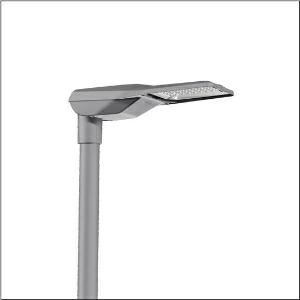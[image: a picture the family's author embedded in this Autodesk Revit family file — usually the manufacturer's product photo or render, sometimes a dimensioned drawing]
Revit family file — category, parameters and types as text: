
# Revit family: streetlight_sl_21_mini___st0_8a_5xe6c43a08gb_7bc1
name_source: partatom
category: Lighting Fixtures
units: mm (PartAtom-declared; Revit-internal decimal feet)

## family parameters
Cut with Voids When Loaded = No
Host = Face
Light Source = No
Part Type = Normal
Room Calculation Point = No
Round Connector Dimension = Use Diameter
Shared = No

## types (1)
- --- (1 x LED, 6180 lm, 40.4 W, 4000K)
    Apparent Load = 40 VA
    CIE Flux Codes = 38 75 97 100 100
    Color Rendering = 70
    Color Temperature = 4000K
    Default Elevation = 1800 mm
    Description = Streetlight SL 21 mini, mast luminaire, primary light control with lens, of PMMA, primary optical cover: cover, of toughened safety glass, transparent, light distribution: ST0.8a, light emission: direct distribution, primary light characteristic: asymmetric, installation type: post-top, side-entry, LED, 3G 1.5mm², High Power LED, rated luminous flux: 6.180lm, luminous efficacy: 153lm/W, light colour: 740, colour temperature: 4000K, control: overheat protection, constant luminous flux control, time-dependent luminous flux control, flexible luminous flux parameterisation, mains connection: 230..240V, AC, 50/60Hz, connection cable pre-assembled, cable length: 6,5m, wiring characteristics: H07RN-F, start of lifetime: 40W, end of service life: 41W, reduction: 19W, luminaire housing, of diecast aluminium, powder-coated, Siteco® metallic grey (DB 702S), corrosivity category C5 mid according to DIN EN ISO 12944, please order mast flange separately, inclination adjustable: 0°, 5°, 10°, 15°, sealing non-destructively replaceable, multi-level sealing system, length: 628mm, width: 235mm, height: 110mm, mast flange for spigot size: 42mm (side-entry): 5XC10008XM4, 60/48mm (side-entry/post-top): 5XC10108XM2, 76/60mm (side-entry/post-top): 5XC10108XM1, protection rating (complete): IP66, insulation class (complete): insulation class II (safety insulation), certification: CE, ENEC, ENEC+, VDE, impact resistance: IK09, permissible operating ambient temperature for outdoor applications: -40..+50°C, standard-compliant lighting for roads and squares, packaging unit: 1 piece

Light Distribution: ST0.8a
    Height = 110 mm
    Lamp = 1 x LED
    Lamp Light Flux = 6180 lm
    Lamp Power = 40.4 W
    Lamp count = 1
    Length = 625 mm
    Luminous efficacy = 153 lm/W
    Manufacturer = Siteco
    ModVariant = No
    Model = 5XE6C43A08GB
    Number of Poles = 1
    OnlyDefault = Yes
    Power Factor = 1
    Product Name = Streetlight SL 21 mini | ST0.8a
    Product group = mast luminaire | pylon top
    ProductGroupID = 6100
    Protection Class = Protection class II
    Protection Degree = IP 66
    RLX_Detail_Level = 1
    RLX_Emergency_Light_Flux = 0 lm
    RLX_Emergency_Type = 0
    RLX_Emergency_Type_DB = No
    RlxData = <blob elided: 92153 chars, md5=d5d46079>
    Socket = socket
    Standby Power = 0 W
    System Light Flux = 6180 lm
    System Power = 40 W
    Type Comments = factory setting: luminous flux: 100 % | Output Level: 100 % | 812 mA
    Type Image = l_1003519.jpg
    URL = http://relux.com
    VarID = @adj_136765
    Voltage = 0 V
    Weight = 0.00 kg
    Width = 234 mm

## geometry (parser evidence)
native form markers: Blend x4, Sweep x11
no freeform markers — native parametric forms only
